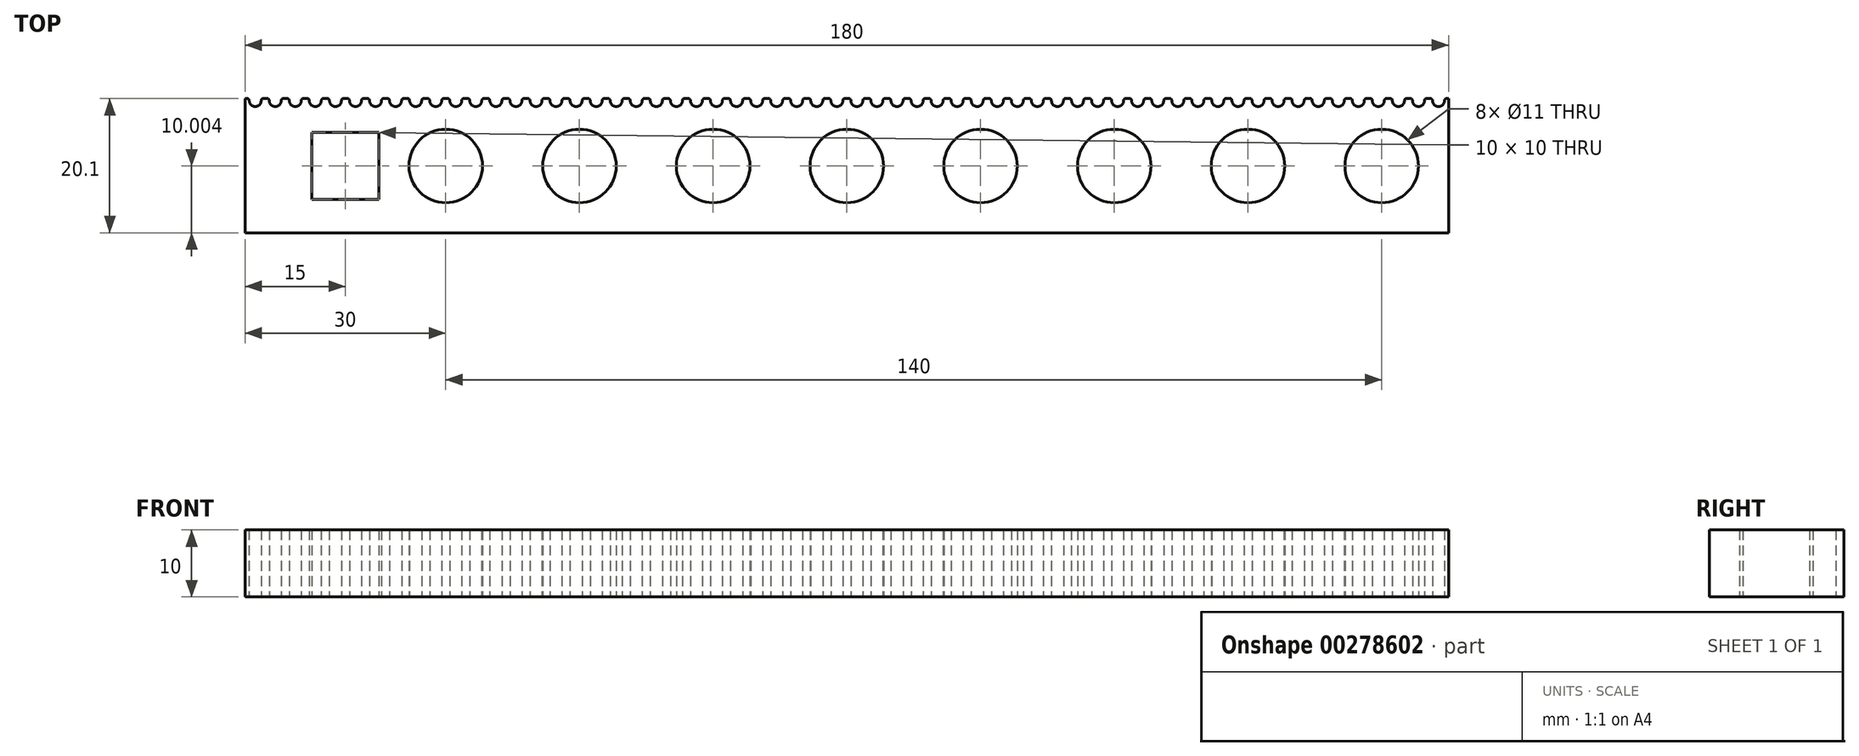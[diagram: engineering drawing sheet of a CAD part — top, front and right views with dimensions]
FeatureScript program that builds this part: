
annotation { "Feature Type Name" : "Feature", "Feature Type Description" : "" }
export const myFeature = defineFeature(function(context is Context, id is Id, definition is map)
    precondition{}
    {
        {
            var Q0;
            Q0=qCreatedBy(makeId("Top.planeOp"),FACE);
            var sketch = newSketch(context, id + "F0", { "sketchPlane" : qUnion([Q0])});
            skLineSegment(sketch, "E0.top", {"start": v(0, -20.1) * mm, "end": v(180, -20.1) * mm});
            skLineSegment(sketch, "E0.left", {"start": v(0, 0) * mm, "end": v(0, -20.1) * mm});
            skLineSegment(sketch, "E0.right", {"start": v(180, 0) * mm, "end": v(180, -20.1) * mm});
            skLineSegment(sketch, "E1", {"start": v(0, -1.2) * mm, "end": v(180, -1.2) * mm});
            skPoint(sketch, "E1.endSnap0", {"position": v(180, -10.05) * mm});
            skLineSegment(sketch, "E2", {"start": v(1.5, 2.44) * mm, "end": v(1.5, -3.97) * mm, "construction": true});
            skPoint(sketch, "E3", {"position": v(1.5, -1.2) * mm});
            skPoint(sketch, "E4", {"position": v(1.5, -0.3) * mm});
            skArc(sketch, "E5", {"start": v(0.6, -0.3) * mm, "mid": v(0.86, -0.94) * mm, "end": v(1.5, -1.2) * mm});
            skPoint(sketch, "E6", {"position": v(0.6, -0.3) * mm});
            skPoint(sketch, "E7", {"position": v(0.3, -0.3) * mm});
            skArc(sketch, "E8", {"start": v(0.6, -0.3) * mm, "mid": v(0.51, -0.09) * mm, "end": v(0.3, 0) * mm});
            skPoint(sketch, "E9", {"position": v(2.4, -0.3) * mm});
            skPoint(sketch, "E10", {"position": v(0.3, 0) * mm});
            skLineSegment(sketch, "E11", {"start": v(0.3, 0) * mm, "end": v(0, 0) * mm});
            skArc(sketch, "E12.MirrorCS", {"start": v(2.4, -0.3) * mm, "mid": v(2.14, -0.94) * mm, "end": v(1.5, -1.2) * mm});
            skArc(sketch, "E13.MirrorCS", {"start": v(2.4, -0.3) * mm, "mid": v(2.49, -0.09) * mm, "end": v(2.7, 0) * mm});
            skLineSegment(sketch, "E14.MirrorCS", {"start": v(2.7, 0) * mm, "end": v(3, 0) * mm});
            skLineSegment(sketch, "E15.1.0.0", {"start": v(3.3, 0) * mm, "end": v(3, 0) * mm});
            skArc(sketch, "E15.1.0.1", {"start": v(3.6, -0.3) * mm, "mid": v(3.51, -0.09) * mm, "end": v(3.3, 0) * mm});
            skArc(sketch, "E15.1.0.2", {"start": v(3.6, -0.3) * mm, "mid": v(3.86, -0.94) * mm, "end": v(4.5, -1.2) * mm});
            skArc(sketch, "E15.1.0.3", {"start": v(5.4, -0.3) * mm, "mid": v(5.14, -0.94) * mm, "end": v(4.5, -1.2) * mm});
            skArc(sketch, "E15.1.0.4", {"start": v(5.4, -0.3) * mm, "mid": v(5.49, -0.09) * mm, "end": v(5.7, 0) * mm});
            skLineSegment(sketch, "E15.1.0.5", {"start": v(5.7, 0) * mm, "end": v(6, 0) * mm});
            skLineSegment(sketch, "E15.2.0.0", {"start": v(6.3, 0) * mm, "end": v(6, 0) * mm});
            skArc(sketch, "E15.2.0.1", {"start": v(6.6, -0.3) * mm, "mid": v(6.51, -0.09) * mm, "end": v(6.3, 0) * mm});
            skArc(sketch, "E15.2.0.2", {"start": v(6.6, -0.3) * mm, "mid": v(6.86, -0.94) * mm, "end": v(7.5, -1.2) * mm});
            skArc(sketch, "E15.2.0.3", {"start": v(8.4, -0.3) * mm, "mid": v(8.14, -0.94) * mm, "end": v(7.5, -1.2) * mm});
            skArc(sketch, "E15.2.0.4", {"start": v(8.4, -0.3) * mm, "mid": v(8.49, -0.09) * mm, "end": v(8.7, 0) * mm});
            skLineSegment(sketch, "E15.2.0.5", {"start": v(8.7, 0) * mm, "end": v(9, 0) * mm});
            skLineSegment(sketch, "E15.3.0.0", {"start": v(9.3, 0) * mm, "end": v(9, 0) * mm});
            skArc(sketch, "E15.3.0.1", {"start": v(9.6, -0.3) * mm, "mid": v(9.51, -0.09) * mm, "end": v(9.3, 0) * mm});
            skArc(sketch, "E15.3.0.2", {"start": v(9.6, -0.3) * mm, "mid": v(9.86, -0.94) * mm, "end": v(10.5, -1.2) * mm});
            skArc(sketch, "E15.3.0.3", {"start": v(11.4, -0.3) * mm, "mid": v(11.14, -0.94) * mm, "end": v(10.5, -1.2) * mm});
            skArc(sketch, "E15.3.0.4", {"start": v(11.4, -0.3) * mm, "mid": v(11.49, -0.09) * mm, "end": v(11.7, 0) * mm});
            skLineSegment(sketch, "E15.3.0.5", {"start": v(11.7, 0) * mm, "end": v(12, 0) * mm});
            skLineSegment(sketch, "E15.4.0.0", {"start": v(12.3, 0) * mm, "end": v(12, 0) * mm});
            skArc(sketch, "E15.4.0.1", {"start": v(12.6, -0.3) * mm, "mid": v(12.51, -0.09) * mm, "end": v(12.3, 0) * mm});
            skArc(sketch, "E15.4.0.2", {"start": v(12.6, -0.3) * mm, "mid": v(12.86, -0.94) * mm, "end": v(13.5, -1.2) * mm});
            skArc(sketch, "E15.4.0.3", {"start": v(14.4, -0.3) * mm, "mid": v(14.14, -0.94) * mm, "end": v(13.5, -1.2) * mm});
            skArc(sketch, "E15.4.0.4", {"start": v(14.4, -0.3) * mm, "mid": v(14.49, -0.09) * mm, "end": v(14.7, 0) * mm});
            skLineSegment(sketch, "E15.4.0.5", {"start": v(14.7, 0) * mm, "end": v(15, 0) * mm});
            skLineSegment(sketch, "E15.5.0.0", {"start": v(15.3, 0) * mm, "end": v(15, 0) * mm});
            skArc(sketch, "E15.5.0.1", {"start": v(15.6, -0.3) * mm, "mid": v(15.51, -0.09) * mm, "end": v(15.3, 0) * mm});
            skArc(sketch, "E15.5.0.2", {"start": v(15.6, -0.3) * mm, "mid": v(15.86, -0.94) * mm, "end": v(16.5, -1.2) * mm});
            skArc(sketch, "E15.5.0.3", {"start": v(17.4, -0.3) * mm, "mid": v(17.14, -0.94) * mm, "end": v(16.5, -1.2) * mm});
            skArc(sketch, "E15.5.0.4", {"start": v(17.4, -0.3) * mm, "mid": v(17.49, -0.09) * mm, "end": v(17.7, 0) * mm});
            skLineSegment(sketch, "E15.5.0.5", {"start": v(17.7, 0) * mm, "end": v(18, 0) * mm});
            skLineSegment(sketch, "E15.6.0.0", {"start": v(18.3, 0) * mm, "end": v(18, 0) * mm});
            skArc(sketch, "E15.6.0.1", {"start": v(18.6, -0.3) * mm, "mid": v(18.51, -0.09) * mm, "end": v(18.3, 0) * mm});
            skArc(sketch, "E15.6.0.2", {"start": v(18.6, -0.3) * mm, "mid": v(18.86, -0.94) * mm, "end": v(19.5, -1.2) * mm});
            skArc(sketch, "E15.6.0.3", {"start": v(20.4, -0.3) * mm, "mid": v(20.14, -0.94) * mm, "end": v(19.5, -1.2) * mm});
            skArc(sketch, "E15.6.0.4", {"start": v(20.4, -0.3) * mm, "mid": v(20.49, -0.09) * mm, "end": v(20.7, 0) * mm});
            skLineSegment(sketch, "E15.6.0.5", {"start": v(20.7, 0) * mm, "end": v(21, 0) * mm});
            skLineSegment(sketch, "E15.7.0.0", {"start": v(21.3, 0) * mm, "end": v(21, 0) * mm});
            skArc(sketch, "E15.7.0.1", {"start": v(21.6, -0.3) * mm, "mid": v(21.51, -0.09) * mm, "end": v(21.3, 0) * mm});
            skArc(sketch, "E15.7.0.2", {"start": v(21.6, -0.3) * mm, "mid": v(21.86, -0.94) * mm, "end": v(22.5, -1.2) * mm});
            skArc(sketch, "E15.7.0.3", {"start": v(23.4, -0.3) * mm, "mid": v(23.14, -0.94) * mm, "end": v(22.5, -1.2) * mm});
            skArc(sketch, "E15.7.0.4", {"start": v(23.4, -0.3) * mm, "mid": v(23.49, -0.09) * mm, "end": v(23.7, 0) * mm});
            skLineSegment(sketch, "E15.7.0.5", {"start": v(23.7, 0) * mm, "end": v(24, 0) * mm});
            skLineSegment(sketch, "E15.8.0.0", {"start": v(24.3, 0) * mm, "end": v(24, 0) * mm});
            skArc(sketch, "E15.8.0.1", {"start": v(24.6, -0.3) * mm, "mid": v(24.51, -0.09) * mm, "end": v(24.3, 0) * mm});
            skArc(sketch, "E15.8.0.2", {"start": v(24.6, -0.3) * mm, "mid": v(24.86, -0.94) * mm, "end": v(25.5, -1.2) * mm});
            skArc(sketch, "E15.8.0.3", {"start": v(26.4, -0.3) * mm, "mid": v(26.14, -0.94) * mm, "end": v(25.5, -1.2) * mm});
            skArc(sketch, "E15.8.0.4", {"start": v(26.4, -0.3) * mm, "mid": v(26.49, -0.09) * mm, "end": v(26.7, 0) * mm});
            skLineSegment(sketch, "E15.8.0.5", {"start": v(26.7, 0) * mm, "end": v(27, 0) * mm});
            skLineSegment(sketch, "E15.9.0.0", {"start": v(27.3, 0) * mm, "end": v(27, 0) * mm});
            skArc(sketch, "E15.9.0.1", {"start": v(27.6, -0.3) * mm, "mid": v(27.51, -0.09) * mm, "end": v(27.3, 0) * mm});
            skArc(sketch, "E15.9.0.2", {"start": v(27.6, -0.3) * mm, "mid": v(27.86, -0.94) * mm, "end": v(28.5, -1.2) * mm});
            skArc(sketch, "E15.9.0.3", {"start": v(29.4, -0.3) * mm, "mid": v(29.14, -0.94) * mm, "end": v(28.5, -1.2) * mm});
            skArc(sketch, "E15.9.0.4", {"start": v(29.4, -0.3) * mm, "mid": v(29.49, -0.09) * mm, "end": v(29.7, 0) * mm});
            skLineSegment(sketch, "E15.9.0.5", {"start": v(29.7, 0) * mm, "end": v(30, 0) * mm});
            skLineSegment(sketch, "E15.10.0.0", {"start": v(30.3, 0) * mm, "end": v(30, 0) * mm});
            skArc(sketch, "E15.10.0.1", {"start": v(30.6, -0.3) * mm, "mid": v(30.51, -0.09) * mm, "end": v(30.3, 0) * mm});
            skArc(sketch, "E15.10.0.2", {"start": v(30.6, -0.3) * mm, "mid": v(30.86, -0.94) * mm, "end": v(31.5, -1.2) * mm});
            skArc(sketch, "E15.10.0.3", {"start": v(32.4, -0.3) * mm, "mid": v(32.14, -0.94) * mm, "end": v(31.5, -1.2) * mm});
            skArc(sketch, "E15.10.0.4", {"start": v(32.4, -0.3) * mm, "mid": v(32.49, -0.09) * mm, "end": v(32.7, 0) * mm});
            skLineSegment(sketch, "E15.10.0.5", {"start": v(32.7, 0) * mm, "end": v(33, 0) * mm});
            skLineSegment(sketch, "E15.11.0.0", {"start": v(33.3, 0) * mm, "end": v(33, 0) * mm});
            skArc(sketch, "E15.11.0.1", {"start": v(33.6, -0.3) * mm, "mid": v(33.51, -0.09) * mm, "end": v(33.3, 0) * mm});
            skArc(sketch, "E15.11.0.2", {"start": v(33.6, -0.3) * mm, "mid": v(33.86, -0.94) * mm, "end": v(34.5, -1.2) * mm});
            skArc(sketch, "E15.11.0.3", {"start": v(35.4, -0.3) * mm, "mid": v(35.14, -0.94) * mm, "end": v(34.5, -1.2) * mm});
            skArc(sketch, "E15.11.0.4", {"start": v(35.4, -0.3) * mm, "mid": v(35.49, -0.09) * mm, "end": v(35.7, 0) * mm});
            skLineSegment(sketch, "E15.11.0.5", {"start": v(35.7, 0) * mm, "end": v(36, 0) * mm});
            skLineSegment(sketch, "E15.12.0.0", {"start": v(36.3, 0) * mm, "end": v(36, 0) * mm});
            skArc(sketch, "E15.12.0.1", {"start": v(36.6, -0.3) * mm, "mid": v(36.51, -0.09) * mm, "end": v(36.3, 0) * mm});
            skArc(sketch, "E15.12.0.2", {"start": v(36.6, -0.3) * mm, "mid": v(36.86, -0.94) * mm, "end": v(37.5, -1.2) * mm});
            skArc(sketch, "E15.12.0.3", {"start": v(38.4, -0.3) * mm, "mid": v(38.14, -0.94) * mm, "end": v(37.5, -1.2) * mm});
            skArc(sketch, "E15.12.0.4", {"start": v(38.4, -0.3) * mm, "mid": v(38.49, -0.09) * mm, "end": v(38.7, 0) * mm});
            skLineSegment(sketch, "E15.12.0.5", {"start": v(38.7, 0) * mm, "end": v(39, 0) * mm});
            skLineSegment(sketch, "E15.13.0.0", {"start": v(39.3, 0) * mm, "end": v(39, 0) * mm});
            skArc(sketch, "E15.13.0.1", {"start": v(39.6, -0.3) * mm, "mid": v(39.51, -0.09) * mm, "end": v(39.3, 0) * mm});
            skArc(sketch, "E15.13.0.2", {"start": v(39.6, -0.3) * mm, "mid": v(39.86, -0.94) * mm, "end": v(40.5, -1.2) * mm});
            skArc(sketch, "E15.13.0.3", {"start": v(41.4, -0.3) * mm, "mid": v(41.14, -0.94) * mm, "end": v(40.5, -1.2) * mm});
            skArc(sketch, "E15.13.0.4", {"start": v(41.4, -0.3) * mm, "mid": v(41.49, -0.09) * mm, "end": v(41.7, 0) * mm});
            skLineSegment(sketch, "E15.13.0.5", {"start": v(41.7, 0) * mm, "end": v(42, 0) * mm});
            skLineSegment(sketch, "E15.14.0.0", {"start": v(42.3, 0) * mm, "end": v(42, 0) * mm});
            skArc(sketch, "E15.14.0.1", {"start": v(42.6, -0.3) * mm, "mid": v(42.51, -0.09) * mm, "end": v(42.3, 0) * mm});
            skArc(sketch, "E15.14.0.2", {"start": v(42.6, -0.3) * mm, "mid": v(42.86, -0.94) * mm, "end": v(43.5, -1.2) * mm});
            skArc(sketch, "E15.14.0.3", {"start": v(44.4, -0.3) * mm, "mid": v(44.14, -0.94) * mm, "end": v(43.5, -1.2) * mm});
            skArc(sketch, "E15.14.0.4", {"start": v(44.4, -0.3) * mm, "mid": v(44.49, -0.09) * mm, "end": v(44.7, 0) * mm});
            skLineSegment(sketch, "E15.14.0.5", {"start": v(44.7, 0) * mm, "end": v(45, 0) * mm});
            skLineSegment(sketch, "E15.15.0.0", {"start": v(45.3, 0) * mm, "end": v(45, 0) * mm});
            skArc(sketch, "E15.15.0.1", {"start": v(45.6, -0.3) * mm, "mid": v(45.51, -0.09) * mm, "end": v(45.3, 0) * mm});
            skArc(sketch, "E15.15.0.2", {"start": v(45.6, -0.3) * mm, "mid": v(45.86, -0.94) * mm, "end": v(46.5, -1.2) * mm});
            skArc(sketch, "E15.15.0.3", {"start": v(47.4, -0.3) * mm, "mid": v(47.14, -0.94) * mm, "end": v(46.5, -1.2) * mm});
            skArc(sketch, "E15.15.0.4", {"start": v(47.4, -0.3) * mm, "mid": v(47.49, -0.09) * mm, "end": v(47.7, 0) * mm});
            skLineSegment(sketch, "E15.15.0.5", {"start": v(47.7, 0) * mm, "end": v(48, 0) * mm});
            skLineSegment(sketch, "E15.16.0.0", {"start": v(48.3, 0) * mm, "end": v(48, 0) * mm});
            skArc(sketch, "E15.16.0.1", {"start": v(48.6, -0.3) * mm, "mid": v(48.51, -0.09) * mm, "end": v(48.3, 0) * mm});
            skArc(sketch, "E15.16.0.2", {"start": v(48.6, -0.3) * mm, "mid": v(48.86, -0.94) * mm, "end": v(49.5, -1.2) * mm});
            skArc(sketch, "E15.16.0.3", {"start": v(50.4, -0.3) * mm, "mid": v(50.14, -0.94) * mm, "end": v(49.5, -1.2) * mm});
            skArc(sketch, "E15.16.0.4", {"start": v(50.4, -0.3) * mm, "mid": v(50.49, -0.09) * mm, "end": v(50.7, 0) * mm});
            skLineSegment(sketch, "E15.16.0.5", {"start": v(50.7, 0) * mm, "end": v(51, 0) * mm});
            skLineSegment(sketch, "E15.17.0.0", {"start": v(51.3, 0) * mm, "end": v(51, 0) * mm});
            skArc(sketch, "E15.17.0.1", {"start": v(51.6, -0.3) * mm, "mid": v(51.51, -0.09) * mm, "end": v(51.3, 0) * mm});
            skArc(sketch, "E15.17.0.2", {"start": v(51.6, -0.3) * mm, "mid": v(51.86, -0.94) * mm, "end": v(52.5, -1.2) * mm});
            skArc(sketch, "E15.17.0.3", {"start": v(53.4, -0.3) * mm, "mid": v(53.14, -0.94) * mm, "end": v(52.5, -1.2) * mm});
            skArc(sketch, "E15.17.0.4", {"start": v(53.4, -0.3) * mm, "mid": v(53.49, -0.09) * mm, "end": v(53.7, 0) * mm});
            skLineSegment(sketch, "E15.17.0.5", {"start": v(53.7, 0) * mm, "end": v(54, 0) * mm});
            skLineSegment(sketch, "E15.18.0.0", {"start": v(54.3, 0) * mm, "end": v(54, 0) * mm});
            skArc(sketch, "E15.18.0.1", {"start": v(54.6, -0.3) * mm, "mid": v(54.51, -0.09) * mm, "end": v(54.3, 0) * mm});
            skArc(sketch, "E15.18.0.2", {"start": v(54.6, -0.3) * mm, "mid": v(54.86, -0.94) * mm, "end": v(55.5, -1.2) * mm});
            skArc(sketch, "E15.18.0.3", {"start": v(56.4, -0.3) * mm, "mid": v(56.14, -0.94) * mm, "end": v(55.5, -1.2) * mm});
            skArc(sketch, "E15.18.0.4", {"start": v(56.4, -0.3) * mm, "mid": v(56.49, -0.09) * mm, "end": v(56.7, 0) * mm});
            skLineSegment(sketch, "E15.18.0.5", {"start": v(56.7, 0) * mm, "end": v(57, 0) * mm});
            skLineSegment(sketch, "E15.19.0.0", {"start": v(57.3, 0) * mm, "end": v(57, 0) * mm});
            skArc(sketch, "E15.19.0.1", {"start": v(57.6, -0.3) * mm, "mid": v(57.51, -0.09) * mm, "end": v(57.3, 0) * mm});
            skArc(sketch, "E15.19.0.2", {"start": v(57.6, -0.3) * mm, "mid": v(57.86, -0.94) * mm, "end": v(58.5, -1.2) * mm});
            skArc(sketch, "E15.19.0.3", {"start": v(59.4, -0.3) * mm, "mid": v(59.14, -0.94) * mm, "end": v(58.5, -1.2) * mm});
            skArc(sketch, "E15.19.0.4", {"start": v(59.4, -0.3) * mm, "mid": v(59.49, -0.09) * mm, "end": v(59.7, 0) * mm});
            skLineSegment(sketch, "E15.19.0.5", {"start": v(59.7, 0) * mm, "end": v(60, 0) * mm});
            skLineSegment(sketch, "E15.20.0.0", {"start": v(60.3, 0) * mm, "end": v(60, 0) * mm});
            skArc(sketch, "E15.20.0.1", {"start": v(60.6, -0.3) * mm, "mid": v(60.51, -0.09) * mm, "end": v(60.3, 0) * mm});
            skArc(sketch, "E15.20.0.2", {"start": v(60.6, -0.3) * mm, "mid": v(60.86, -0.94) * mm, "end": v(61.5, -1.2) * mm});
            skArc(sketch, "E15.20.0.3", {"start": v(62.4, -0.3) * mm, "mid": v(62.14, -0.94) * mm, "end": v(61.5, -1.2) * mm});
            skArc(sketch, "E15.20.0.4", {"start": v(62.4, -0.3) * mm, "mid": v(62.49, -0.09) * mm, "end": v(62.7, 0) * mm});
            skLineSegment(sketch, "E15.20.0.5", {"start": v(62.7, 0) * mm, "end": v(63, 0) * mm});
            skLineSegment(sketch, "E15.21.0.0", {"start": v(63.3, 0) * mm, "end": v(63, 0) * mm});
            skArc(sketch, "E15.21.0.1", {"start": v(63.6, -0.3) * mm, "mid": v(63.51, -0.09) * mm, "end": v(63.3, 0) * mm});
            skArc(sketch, "E15.21.0.2", {"start": v(63.6, -0.3) * mm, "mid": v(63.86, -0.94) * mm, "end": v(64.5, -1.2) * mm});
            skArc(sketch, "E15.21.0.3", {"start": v(65.4, -0.3) * mm, "mid": v(65.14, -0.94) * mm, "end": v(64.5, -1.2) * mm});
            skArc(sketch, "E15.21.0.4", {"start": v(65.4, -0.3) * mm, "mid": v(65.49, -0.09) * mm, "end": v(65.7, 0) * mm});
            skLineSegment(sketch, "E15.21.0.5", {"start": v(65.7, 0) * mm, "end": v(66, 0) * mm});
            skLineSegment(sketch, "E15.22.0.0", {"start": v(66.3, 0) * mm, "end": v(66, 0) * mm});
            skArc(sketch, "E15.22.0.1", {"start": v(66.6, -0.3) * mm, "mid": v(66.51, -0.09) * mm, "end": v(66.3, 0) * mm});
            skArc(sketch, "E15.22.0.2", {"start": v(66.6, -0.3) * mm, "mid": v(66.86, -0.94) * mm, "end": v(67.5, -1.2) * mm});
            skArc(sketch, "E15.22.0.3", {"start": v(68.4, -0.3) * mm, "mid": v(68.14, -0.94) * mm, "end": v(67.5, -1.2) * mm});
            skArc(sketch, "E15.22.0.4", {"start": v(68.4, -0.3) * mm, "mid": v(68.49, -0.09) * mm, "end": v(68.7, 0) * mm});
            skLineSegment(sketch, "E15.22.0.5", {"start": v(68.7, 0) * mm, "end": v(69, 0) * mm});
            skLineSegment(sketch, "E15.23.0.0", {"start": v(69.3, 0) * mm, "end": v(69, 0) * mm});
            skArc(sketch, "E15.23.0.1", {"start": v(69.6, -0.3) * mm, "mid": v(69.51, -0.09) * mm, "end": v(69.3, 0) * mm});
            skArc(sketch, "E15.23.0.2", {"start": v(69.6, -0.3) * mm, "mid": v(69.86, -0.94) * mm, "end": v(70.5, -1.2) * mm});
            skArc(sketch, "E15.23.0.3", {"start": v(71.4, -0.3) * mm, "mid": v(71.14, -0.94) * mm, "end": v(70.5, -1.2) * mm});
            skArc(sketch, "E15.23.0.4", {"start": v(71.4, -0.3) * mm, "mid": v(71.49, -0.09) * mm, "end": v(71.7, 0) * mm});
            skLineSegment(sketch, "E15.23.0.5", {"start": v(71.7, 0) * mm, "end": v(72, 0) * mm});
            skLineSegment(sketch, "E15.24.0.0", {"start": v(72.3, 0) * mm, "end": v(72, 0) * mm});
            skArc(sketch, "E15.24.0.1", {"start": v(72.6, -0.3) * mm, "mid": v(72.51, -0.09) * mm, "end": v(72.3, 0) * mm});
            skArc(sketch, "E15.24.0.2", {"start": v(72.6, -0.3) * mm, "mid": v(72.86, -0.94) * mm, "end": v(73.5, -1.2) * mm});
            skArc(sketch, "E15.24.0.3", {"start": v(74.4, -0.3) * mm, "mid": v(74.14, -0.94) * mm, "end": v(73.5, -1.2) * mm});
            skArc(sketch, "E15.24.0.4", {"start": v(74.4, -0.3) * mm, "mid": v(74.49, -0.09) * mm, "end": v(74.7, 0) * mm});
            skLineSegment(sketch, "E15.24.0.5", {"start": v(74.7, 0) * mm, "end": v(75, 0) * mm});
            skLineSegment(sketch, "E15.25.0.0", {"start": v(75.3, 0) * mm, "end": v(75, 0) * mm});
            skArc(sketch, "E15.25.0.1", {"start": v(75.6, -0.3) * mm, "mid": v(75.51, -0.09) * mm, "end": v(75.3, 0) * mm});
            skArc(sketch, "E15.25.0.2", {"start": v(75.6, -0.3) * mm, "mid": v(75.86, -0.94) * mm, "end": v(76.5, -1.2) * mm});
            skArc(sketch, "E15.25.0.3", {"start": v(77.4, -0.3) * mm, "mid": v(77.14, -0.94) * mm, "end": v(76.5, -1.2) * mm});
            skArc(sketch, "E15.25.0.4", {"start": v(77.4, -0.3) * mm, "mid": v(77.49, -0.09) * mm, "end": v(77.7, 0) * mm});
            skLineSegment(sketch, "E15.25.0.5", {"start": v(77.7, 0) * mm, "end": v(78, 0) * mm});
            skLineSegment(sketch, "E15.26.0.0", {"start": v(78.3, 0) * mm, "end": v(78, 0) * mm});
            skArc(sketch, "E15.26.0.1", {"start": v(78.6, -0.3) * mm, "mid": v(78.51, -0.09) * mm, "end": v(78.3, 0) * mm});
            skArc(sketch, "E15.26.0.2", {"start": v(78.6, -0.3) * mm, "mid": v(78.86, -0.94) * mm, "end": v(79.5, -1.2) * mm});
            skArc(sketch, "E15.26.0.3", {"start": v(80.4, -0.3) * mm, "mid": v(80.14, -0.94) * mm, "end": v(79.5, -1.2) * mm});
            skArc(sketch, "E15.26.0.4", {"start": v(80.4, -0.3) * mm, "mid": v(80.49, -0.09) * mm, "end": v(80.7, 0) * mm});
            skLineSegment(sketch, "E15.26.0.5", {"start": v(80.7, 0) * mm, "end": v(81, 0) * mm});
            skLineSegment(sketch, "E15.27.0.0", {"start": v(81.3, 0) * mm, "end": v(81, 0) * mm});
            skArc(sketch, "E15.27.0.1", {"start": v(81.6, -0.3) * mm, "mid": v(81.51, -0.09) * mm, "end": v(81.3, 0) * mm});
            skArc(sketch, "E15.27.0.2", {"start": v(81.6, -0.3) * mm, "mid": v(81.86, -0.94) * mm, "end": v(82.5, -1.2) * mm});
            skArc(sketch, "E15.27.0.3", {"start": v(83.4, -0.3) * mm, "mid": v(83.14, -0.94) * mm, "end": v(82.5, -1.2) * mm});
            skArc(sketch, "E15.27.0.4", {"start": v(83.4, -0.3) * mm, "mid": v(83.49, -0.09) * mm, "end": v(83.7, 0) * mm});
            skLineSegment(sketch, "E15.27.0.5", {"start": v(83.7, 0) * mm, "end": v(84, 0) * mm});
            skLineSegment(sketch, "E15.28.0.0", {"start": v(84.3, 0) * mm, "end": v(84, 0) * mm});
            skArc(sketch, "E15.28.0.1", {"start": v(84.6, -0.3) * mm, "mid": v(84.51, -0.09) * mm, "end": v(84.3, 0) * mm});
            skArc(sketch, "E15.28.0.2", {"start": v(84.6, -0.3) * mm, "mid": v(84.86, -0.94) * mm, "end": v(85.5, -1.2) * mm});
            skArc(sketch, "E15.28.0.3", {"start": v(86.4, -0.3) * mm, "mid": v(86.14, -0.94) * mm, "end": v(85.5, -1.2) * mm});
            skArc(sketch, "E15.28.0.4", {"start": v(86.4, -0.3) * mm, "mid": v(86.49, -0.09) * mm, "end": v(86.7, 0) * mm});
            skLineSegment(sketch, "E15.28.0.5", {"start": v(86.7, 0) * mm, "end": v(87, 0) * mm});
            skLineSegment(sketch, "E15.29.0.0", {"start": v(87.3, 0) * mm, "end": v(87, 0) * mm});
            skArc(sketch, "E15.29.0.1", {"start": v(87.6, -0.3) * mm, "mid": v(87.51, -0.09) * mm, "end": v(87.3, 0) * mm});
            skArc(sketch, "E15.29.0.2", {"start": v(87.6, -0.3) * mm, "mid": v(87.86, -0.94) * mm, "end": v(88.5, -1.2) * mm});
            skArc(sketch, "E15.29.0.3", {"start": v(89.4, -0.3) * mm, "mid": v(89.14, -0.94) * mm, "end": v(88.5, -1.2) * mm});
            skArc(sketch, "E15.29.0.4", {"start": v(89.4, -0.3) * mm, "mid": v(89.49, -0.09) * mm, "end": v(89.7, 0) * mm});
            skLineSegment(sketch, "E15.29.0.5", {"start": v(89.7, 0) * mm, "end": v(90, 0) * mm});
            skLineSegment(sketch, "E15.30.0.0", {"start": v(90.3, 0) * mm, "end": v(90, 0) * mm});
            skArc(sketch, "E15.30.0.1", {"start": v(90.6, -0.3) * mm, "mid": v(90.51, -0.09) * mm, "end": v(90.3, 0) * mm});
            skArc(sketch, "E15.30.0.2", {"start": v(90.6, -0.3) * mm, "mid": v(90.86, -0.94) * mm, "end": v(91.5, -1.2) * mm});
            skArc(sketch, "E15.30.0.3", {"start": v(92.4, -0.3) * mm, "mid": v(92.14, -0.94) * mm, "end": v(91.5, -1.2) * mm});
            skArc(sketch, "E15.30.0.4", {"start": v(92.4, -0.3) * mm, "mid": v(92.49, -0.09) * mm, "end": v(92.7, 0) * mm});
            skLineSegment(sketch, "E15.30.0.5", {"start": v(92.7, 0) * mm, "end": v(93, 0) * mm});
            skLineSegment(sketch, "E15.31.0.0", {"start": v(93.3, 0) * mm, "end": v(93, 0) * mm});
            skArc(sketch, "E15.31.0.1", {"start": v(93.6, -0.3) * mm, "mid": v(93.51, -0.09) * mm, "end": v(93.3, 0) * mm});
            skArc(sketch, "E15.31.0.2", {"start": v(93.6, -0.3) * mm, "mid": v(93.86, -0.94) * mm, "end": v(94.5, -1.2) * mm});
            skArc(sketch, "E15.31.0.3", {"start": v(95.4, -0.3) * mm, "mid": v(95.14, -0.94) * mm, "end": v(94.5, -1.2) * mm});
            skArc(sketch, "E15.31.0.4", {"start": v(95.4, -0.3) * mm, "mid": v(95.49, -0.09) * mm, "end": v(95.7, 0) * mm});
            skLineSegment(sketch, "E15.31.0.5", {"start": v(95.7, 0) * mm, "end": v(96, 0) * mm});
            skLineSegment(sketch, "E15.32.0.0", {"start": v(96.3, 0) * mm, "end": v(96, 0) * mm});
            skArc(sketch, "E15.32.0.1", {"start": v(96.6, -0.3) * mm, "mid": v(96.51, -0.09) * mm, "end": v(96.3, 0) * mm});
            skArc(sketch, "E15.32.0.2", {"start": v(96.6, -0.3) * mm, "mid": v(96.86, -0.94) * mm, "end": v(97.5, -1.2) * mm});
            skArc(sketch, "E15.32.0.3", {"start": v(98.4, -0.3) * mm, "mid": v(98.14, -0.94) * mm, "end": v(97.5, -1.2) * mm});
            skArc(sketch, "E15.32.0.4", {"start": v(98.4, -0.3) * mm, "mid": v(98.49, -0.09) * mm, "end": v(98.7, 0) * mm});
            skLineSegment(sketch, "E15.32.0.5", {"start": v(98.7, 0) * mm, "end": v(99, 0) * mm});
            skLineSegment(sketch, "E15.33.0.0", {"start": v(99.3, 0) * mm, "end": v(99, 0) * mm});
            skArc(sketch, "E15.33.0.1", {"start": v(99.6, -0.3) * mm, "mid": v(99.51, -0.09) * mm, "end": v(99.3, 0) * mm});
            skArc(sketch, "E15.33.0.2", {"start": v(99.6, -0.3) * mm, "mid": v(99.86, -0.94) * mm, "end": v(100.5, -1.2) * mm});
            skArc(sketch, "E15.33.0.3", {"start": v(101.4, -0.3) * mm, "mid": v(101.14, -0.94) * mm, "end": v(100.5, -1.2) * mm});
            skArc(sketch, "E15.33.0.4", {"start": v(101.4, -0.3) * mm, "mid": v(101.49, -0.09) * mm, "end": v(101.7, 0) * mm});
            skLineSegment(sketch, "E15.33.0.5", {"start": v(101.7, 0) * mm, "end": v(102, 0) * mm});
            skLineSegment(sketch, "E15.34.0.0", {"start": v(102.3, 0) * mm, "end": v(102, 0) * mm});
            skArc(sketch, "E15.34.0.1", {"start": v(102.6, -0.3) * mm, "mid": v(102.51, -0.09) * mm, "end": v(102.3, 0) * mm});
            skArc(sketch, "E15.34.0.2", {"start": v(102.6, -0.3) * mm, "mid": v(102.86, -0.94) * mm, "end": v(103.5, -1.2) * mm});
            skArc(sketch, "E15.34.0.3", {"start": v(104.4, -0.3) * mm, "mid": v(104.14, -0.94) * mm, "end": v(103.5, -1.2) * mm});
            skArc(sketch, "E15.34.0.4", {"start": v(104.4, -0.3) * mm, "mid": v(104.49, -0.09) * mm, "end": v(104.7, 0) * mm});
            skLineSegment(sketch, "E15.34.0.5", {"start": v(104.7, 0) * mm, "end": v(105, 0) * mm});
            skLineSegment(sketch, "E15.35.0.0", {"start": v(105.3, 0) * mm, "end": v(105, 0) * mm});
            skArc(sketch, "E15.35.0.1", {"start": v(105.6, -0.3) * mm, "mid": v(105.51, -0.09) * mm, "end": v(105.3, 0) * mm});
            skArc(sketch, "E15.35.0.2", {"start": v(105.6, -0.3) * mm, "mid": v(105.86, -0.94) * mm, "end": v(106.5, -1.2) * mm});
            skArc(sketch, "E15.35.0.3", {"start": v(107.4, -0.3) * mm, "mid": v(107.14, -0.94) * mm, "end": v(106.5, -1.2) * mm});
            skArc(sketch, "E15.35.0.4", {"start": v(107.4, -0.3) * mm, "mid": v(107.49, -0.09) * mm, "end": v(107.7, 0) * mm});
            skLineSegment(sketch, "E15.35.0.5", {"start": v(107.7, 0) * mm, "end": v(108, 0) * mm});
            skLineSegment(sketch, "E15.36.0.0", {"start": v(108.3, 0) * mm, "end": v(108, 0) * mm});
            skArc(sketch, "E15.36.0.1", {"start": v(108.6, -0.3) * mm, "mid": v(108.51, -0.09) * mm, "end": v(108.3, 0) * mm});
            skArc(sketch, "E15.36.0.2", {"start": v(108.6, -0.3) * mm, "mid": v(108.86, -0.94) * mm, "end": v(109.5, -1.2) * mm});
            skArc(sketch, "E15.36.0.3", {"start": v(110.4, -0.3) * mm, "mid": v(110.14, -0.94) * mm, "end": v(109.5, -1.2) * mm});
            skArc(sketch, "E15.36.0.4", {"start": v(110.4, -0.3) * mm, "mid": v(110.49, -0.09) * mm, "end": v(110.7, 0) * mm});
            skLineSegment(sketch, "E15.36.0.5", {"start": v(110.7, 0) * mm, "end": v(111, 0) * mm});
            skLineSegment(sketch, "E15.37.0.0", {"start": v(111.3, 0) * mm, "end": v(111, 0) * mm});
            skArc(sketch, "E15.37.0.1", {"start": v(111.6, -0.3) * mm, "mid": v(111.51, -0.09) * mm, "end": v(111.3, 0) * mm});
            skArc(sketch, "E15.37.0.2", {"start": v(111.6, -0.3) * mm, "mid": v(111.86, -0.94) * mm, "end": v(112.5, -1.2) * mm});
            skArc(sketch, "E15.37.0.3", {"start": v(113.4, -0.3) * mm, "mid": v(113.14, -0.94) * mm, "end": v(112.5, -1.2) * mm});
            skArc(sketch, "E15.37.0.4", {"start": v(113.4, -0.3) * mm, "mid": v(113.49, -0.09) * mm, "end": v(113.7, 0) * mm});
            skLineSegment(sketch, "E15.37.0.5", {"start": v(113.7, 0) * mm, "end": v(114, 0) * mm});
            skLineSegment(sketch, "E15.38.0.0", {"start": v(114.3, 0) * mm, "end": v(114, 0) * mm});
            skArc(sketch, "E15.38.0.1", {"start": v(114.6, -0.3) * mm, "mid": v(114.51, -0.09) * mm, "end": v(114.3, 0) * mm});
            skArc(sketch, "E15.38.0.2", {"start": v(114.6, -0.3) * mm, "mid": v(114.86, -0.94) * mm, "end": v(115.5, -1.2) * mm});
            skArc(sketch, "E15.38.0.3", {"start": v(116.4, -0.3) * mm, "mid": v(116.14, -0.94) * mm, "end": v(115.5, -1.2) * mm});
            skArc(sketch, "E15.38.0.4", {"start": v(116.4, -0.3) * mm, "mid": v(116.49, -0.09) * mm, "end": v(116.7, 0) * mm});
            skLineSegment(sketch, "E15.38.0.5", {"start": v(116.7, 0) * mm, "end": v(117, 0) * mm});
            skLineSegment(sketch, "E15.39.0.0", {"start": v(117.3, 0) * mm, "end": v(117, 0) * mm});
            skArc(sketch, "E15.39.0.1", {"start": v(117.6, -0.3) * mm, "mid": v(117.51, -0.09) * mm, "end": v(117.3, 0) * mm});
            skArc(sketch, "E15.39.0.2", {"start": v(117.6, -0.3) * mm, "mid": v(117.86, -0.94) * mm, "end": v(118.5, -1.2) * mm});
            skArc(sketch, "E15.39.0.3", {"start": v(119.4, -0.3) * mm, "mid": v(119.14, -0.94) * mm, "end": v(118.5, -1.2) * mm});
            skArc(sketch, "E15.39.0.4", {"start": v(119.4, -0.3) * mm, "mid": v(119.49, -0.09) * mm, "end": v(119.7, 0) * mm});
            skLineSegment(sketch, "E15.39.0.5", {"start": v(119.7, 0) * mm, "end": v(120, 0) * mm});
            skLineSegment(sketch, "E15.40.0.0", {"start": v(120.3, 0) * mm, "end": v(120, 0) * mm});
            skArc(sketch, "E15.40.0.1", {"start": v(120.6, -0.3) * mm, "mid": v(120.51, -0.09) * mm, "end": v(120.3, 0) * mm});
            skArc(sketch, "E15.40.0.2", {"start": v(120.6, -0.3) * mm, "mid": v(120.86, -0.94) * mm, "end": v(121.5, -1.2) * mm});
            skArc(sketch, "E15.40.0.3", {"start": v(122.4, -0.3) * mm, "mid": v(122.14, -0.94) * mm, "end": v(121.5, -1.2) * mm});
            skArc(sketch, "E15.40.0.4", {"start": v(122.4, -0.3) * mm, "mid": v(122.49, -0.09) * mm, "end": v(122.7, 0) * mm});
            skLineSegment(sketch, "E15.40.0.5", {"start": v(122.7, 0) * mm, "end": v(123, 0) * mm});
            skLineSegment(sketch, "E15.41.0.0", {"start": v(123.3, 0) * mm, "end": v(123, 0) * mm});
            skArc(sketch, "E15.41.0.1", {"start": v(123.6, -0.3) * mm, "mid": v(123.51, -0.09) * mm, "end": v(123.3, 0) * mm});
            skArc(sketch, "E15.41.0.2", {"start": v(123.6, -0.3) * mm, "mid": v(123.86, -0.94) * mm, "end": v(124.5, -1.2) * mm});
            skArc(sketch, "E15.41.0.3", {"start": v(125.4, -0.3) * mm, "mid": v(125.14, -0.94) * mm, "end": v(124.5, -1.2) * mm});
            skArc(sketch, "E15.41.0.4", {"start": v(125.4, -0.3) * mm, "mid": v(125.49, -0.09) * mm, "end": v(125.7, 0) * mm});
            skLineSegment(sketch, "E15.41.0.5", {"start": v(125.7, 0) * mm, "end": v(126, 0) * mm});
            skLineSegment(sketch, "E15.42.0.0", {"start": v(126.3, 0) * mm, "end": v(126, 0) * mm});
            skArc(sketch, "E15.42.0.1", {"start": v(126.6, -0.3) * mm, "mid": v(126.51, -0.09) * mm, "end": v(126.3, 0) * mm});
            skArc(sketch, "E15.42.0.2", {"start": v(126.6, -0.3) * mm, "mid": v(126.86, -0.94) * mm, "end": v(127.5, -1.2) * mm});
            skArc(sketch, "E15.42.0.3", {"start": v(128.4, -0.3) * mm, "mid": v(128.14, -0.94) * mm, "end": v(127.5, -1.2) * mm});
            skArc(sketch, "E15.42.0.4", {"start": v(128.4, -0.3) * mm, "mid": v(128.49, -0.09) * mm, "end": v(128.7, 0) * mm});
            skLineSegment(sketch, "E15.42.0.5", {"start": v(128.7, 0) * mm, "end": v(129, 0) * mm});
            skLineSegment(sketch, "E15.43.0.0", {"start": v(129.3, 0) * mm, "end": v(129, 0) * mm});
            skArc(sketch, "E15.43.0.1", {"start": v(129.6, -0.3) * mm, "mid": v(129.51, -0.09) * mm, "end": v(129.3, 0) * mm});
            skArc(sketch, "E15.43.0.2", {"start": v(129.6, -0.3) * mm, "mid": v(129.86, -0.94) * mm, "end": v(130.5, -1.2) * mm});
            skArc(sketch, "E15.43.0.3", {"start": v(131.4, -0.3) * mm, "mid": v(131.14, -0.94) * mm, "end": v(130.5, -1.2) * mm});
            skArc(sketch, "E15.43.0.4", {"start": v(131.4, -0.3) * mm, "mid": v(131.49, -0.09) * mm, "end": v(131.7, 0) * mm});
            skLineSegment(sketch, "E15.43.0.5", {"start": v(131.7, 0) * mm, "end": v(132, 0) * mm});
            skLineSegment(sketch, "E15.44.0.0", {"start": v(132.3, 0) * mm, "end": v(132, 0) * mm});
            skArc(sketch, "E15.44.0.1", {"start": v(132.6, -0.3) * mm, "mid": v(132.51, -0.09) * mm, "end": v(132.3, 0) * mm});
            skArc(sketch, "E15.44.0.2", {"start": v(132.6, -0.3) * mm, "mid": v(132.86, -0.94) * mm, "end": v(133.5, -1.2) * mm});
            skArc(sketch, "E15.44.0.3", {"start": v(134.4, -0.3) * mm, "mid": v(134.14, -0.94) * mm, "end": v(133.5, -1.2) * mm});
            skArc(sketch, "E15.44.0.4", {"start": v(134.4, -0.3) * mm, "mid": v(134.49, -0.09) * mm, "end": v(134.7, 0) * mm});
            skLineSegment(sketch, "E15.44.0.5", {"start": v(134.7, 0) * mm, "end": v(135, 0) * mm});
            skLineSegment(sketch, "E15.45.0.0", {"start": v(135.3, 0) * mm, "end": v(135, 0) * mm});
            skArc(sketch, "E15.45.0.1", {"start": v(135.6, -0.3) * mm, "mid": v(135.51, -0.09) * mm, "end": v(135.3, 0) * mm});
            skArc(sketch, "E15.45.0.2", {"start": v(135.6, -0.3) * mm, "mid": v(135.86, -0.94) * mm, "end": v(136.5, -1.2) * mm});
            skArc(sketch, "E15.45.0.3", {"start": v(137.4, -0.3) * mm, "mid": v(137.14, -0.94) * mm, "end": v(136.5, -1.2) * mm});
            skArc(sketch, "E15.45.0.4", {"start": v(137.4, -0.3) * mm, "mid": v(137.49, -0.09) * mm, "end": v(137.7, 0) * mm});
            skLineSegment(sketch, "E15.45.0.5", {"start": v(137.7, 0) * mm, "end": v(138, 0) * mm});
            skLineSegment(sketch, "E15.46.0.0", {"start": v(138.3, 0) * mm, "end": v(138, 0) * mm});
            skArc(sketch, "E15.46.0.1", {"start": v(138.6, -0.3) * mm, "mid": v(138.51, -0.09) * mm, "end": v(138.3, 0) * mm});
            skArc(sketch, "E15.46.0.2", {"start": v(138.6, -0.3) * mm, "mid": v(138.86, -0.94) * mm, "end": v(139.5, -1.2) * mm});
            skArc(sketch, "E15.46.0.3", {"start": v(140.4, -0.3) * mm, "mid": v(140.14, -0.94) * mm, "end": v(139.5, -1.2) * mm});
            skArc(sketch, "E15.46.0.4", {"start": v(140.4, -0.3) * mm, "mid": v(140.49, -0.09) * mm, "end": v(140.7, 0) * mm});
            skLineSegment(sketch, "E15.46.0.5", {"start": v(140.7, 0) * mm, "end": v(141, 0) * mm});
            skLineSegment(sketch, "E15.47.0.0", {"start": v(141.3, 0) * mm, "end": v(141, 0) * mm});
            skArc(sketch, "E15.47.0.1", {"start": v(141.6, -0.3) * mm, "mid": v(141.51, -0.09) * mm, "end": v(141.3, 0) * mm});
            skArc(sketch, "E15.47.0.2", {"start": v(141.6, -0.3) * mm, "mid": v(141.86, -0.94) * mm, "end": v(142.5, -1.2) * mm});
            skArc(sketch, "E15.47.0.3", {"start": v(143.4, -0.3) * mm, "mid": v(143.14, -0.94) * mm, "end": v(142.5, -1.2) * mm});
            skArc(sketch, "E15.47.0.4", {"start": v(143.4, -0.3) * mm, "mid": v(143.49, -0.09) * mm, "end": v(143.7, 0) * mm});
            skLineSegment(sketch, "E15.47.0.5", {"start": v(143.7, 0) * mm, "end": v(144, 0) * mm});
            skLineSegment(sketch, "E15.48.0.0", {"start": v(144.3, 0) * mm, "end": v(144, 0) * mm});
            skArc(sketch, "E15.48.0.1", {"start": v(144.6, -0.3) * mm, "mid": v(144.51, -0.09) * mm, "end": v(144.3, 0) * mm});
            skArc(sketch, "E15.48.0.2", {"start": v(144.6, -0.3) * mm, "mid": v(144.86, -0.94) * mm, "end": v(145.5, -1.2) * mm});
            skArc(sketch, "E15.48.0.3", {"start": v(146.4, -0.3) * mm, "mid": v(146.14, -0.94) * mm, "end": v(145.5, -1.2) * mm});
            skArc(sketch, "E15.48.0.4", {"start": v(146.4, -0.3) * mm, "mid": v(146.49, -0.09) * mm, "end": v(146.7, 0) * mm});
            skLineSegment(sketch, "E15.48.0.5", {"start": v(146.7, 0) * mm, "end": v(147, 0) * mm});
            skLineSegment(sketch, "E15.49.0.0", {"start": v(147.3, 0) * mm, "end": v(147, 0) * mm});
            skArc(sketch, "E15.49.0.1", {"start": v(147.6, -0.3) * mm, "mid": v(147.51, -0.09) * mm, "end": v(147.3, 0) * mm});
            skArc(sketch, "E15.49.0.2", {"start": v(147.6, -0.3) * mm, "mid": v(147.86, -0.94) * mm, "end": v(148.5, -1.2) * mm});
            skArc(sketch, "E15.49.0.3", {"start": v(149.4, -0.3) * mm, "mid": v(149.14, -0.94) * mm, "end": v(148.5, -1.2) * mm});
            skArc(sketch, "E15.49.0.4", {"start": v(149.4, -0.3) * mm, "mid": v(149.49, -0.09) * mm, "end": v(149.7, 0) * mm});
            skLineSegment(sketch, "E15.49.0.5", {"start": v(149.7, 0) * mm, "end": v(150, 0) * mm});
            skLineSegment(sketch, "E15.50.0.0", {"start": v(150.3, 0) * mm, "end": v(150, 0) * mm});
            skArc(sketch, "E15.50.0.1", {"start": v(150.6, -0.3) * mm, "mid": v(150.51, -0.09) * mm, "end": v(150.3, 0) * mm});
            skArc(sketch, "E15.50.0.2", {"start": v(150.6, -0.3) * mm, "mid": v(150.86, -0.94) * mm, "end": v(151.5, -1.2) * mm});
            skArc(sketch, "E15.50.0.3", {"start": v(152.4, -0.3) * mm, "mid": v(152.14, -0.94) * mm, "end": v(151.5, -1.2) * mm});
            skArc(sketch, "E15.50.0.4", {"start": v(152.4, -0.3) * mm, "mid": v(152.49, -0.09) * mm, "end": v(152.7, 0) * mm});
            skLineSegment(sketch, "E15.50.0.5", {"start": v(152.7, 0) * mm, "end": v(153, 0) * mm});
            skLineSegment(sketch, "E15.51.0.0", {"start": v(153.3, 0) * mm, "end": v(153, 0) * mm});
            skArc(sketch, "E15.51.0.1", {"start": v(153.6, -0.3) * mm, "mid": v(153.51, -0.09) * mm, "end": v(153.3, 0) * mm});
            skArc(sketch, "E15.51.0.2", {"start": v(153.6, -0.3) * mm, "mid": v(153.86, -0.94) * mm, "end": v(154.5, -1.2) * mm});
            skArc(sketch, "E15.51.0.3", {"start": v(155.4, -0.3) * mm, "mid": v(155.14, -0.94) * mm, "end": v(154.5, -1.2) * mm});
            skArc(sketch, "E15.51.0.4", {"start": v(155.4, -0.3) * mm, "mid": v(155.49, -0.09) * mm, "end": v(155.7, 0) * mm});
            skLineSegment(sketch, "E15.51.0.5", {"start": v(155.7, 0) * mm, "end": v(156, 0) * mm});
            skLineSegment(sketch, "E15.52.0.0", {"start": v(156.3, 0) * mm, "end": v(156, 0) * mm});
            skArc(sketch, "E15.52.0.1", {"start": v(156.6, -0.3) * mm, "mid": v(156.51, -0.09) * mm, "end": v(156.3, 0) * mm});
            skArc(sketch, "E15.52.0.2", {"start": v(156.6, -0.3) * mm, "mid": v(156.86, -0.94) * mm, "end": v(157.5, -1.2) * mm});
            skArc(sketch, "E15.52.0.3", {"start": v(158.4, -0.3) * mm, "mid": v(158.14, -0.94) * mm, "end": v(157.5, -1.2) * mm});
            skArc(sketch, "E15.52.0.4", {"start": v(158.4, -0.3) * mm, "mid": v(158.49, -0.09) * mm, "end": v(158.7, 0) * mm});
            skLineSegment(sketch, "E15.52.0.5", {"start": v(158.7, 0) * mm, "end": v(159, 0) * mm});
            skLineSegment(sketch, "E15.53.0.0", {"start": v(159.3, 0) * mm, "end": v(159, 0) * mm});
            skArc(sketch, "E15.53.0.1", {"start": v(159.6, -0.3) * mm, "mid": v(159.51, -0.09) * mm, "end": v(159.3, 0) * mm});
            skArc(sketch, "E15.53.0.2", {"start": v(159.6, -0.3) * mm, "mid": v(159.86, -0.94) * mm, "end": v(160.5, -1.2) * mm});
            skArc(sketch, "E15.53.0.3", {"start": v(161.4, -0.3) * mm, "mid": v(161.14, -0.94) * mm, "end": v(160.5, -1.2) * mm});
            skArc(sketch, "E15.53.0.4", {"start": v(161.4, -0.3) * mm, "mid": v(161.49, -0.09) * mm, "end": v(161.7, 0) * mm});
            skLineSegment(sketch, "E15.53.0.5", {"start": v(161.7, 0) * mm, "end": v(162, 0) * mm});
            skLineSegment(sketch, "E15.54.0.0", {"start": v(162.3, 0) * mm, "end": v(162, 0) * mm});
            skArc(sketch, "E15.54.0.1", {"start": v(162.6, -0.3) * mm, "mid": v(162.51, -0.09) * mm, "end": v(162.3, 0) * mm});
            skArc(sketch, "E15.54.0.2", {"start": v(162.6, -0.3) * mm, "mid": v(162.86, -0.94) * mm, "end": v(163.5, -1.2) * mm});
            skArc(sketch, "E15.54.0.3", {"start": v(164.4, -0.3) * mm, "mid": v(164.14, -0.94) * mm, "end": v(163.5, -1.2) * mm});
            skArc(sketch, "E15.54.0.4", {"start": v(164.4, -0.3) * mm, "mid": v(164.49, -0.09) * mm, "end": v(164.7, 0) * mm});
            skLineSegment(sketch, "E15.54.0.5", {"start": v(164.7, 0) * mm, "end": v(165, 0) * mm});
            skLineSegment(sketch, "E15.55.0.0", {"start": v(165.3, 0) * mm, "end": v(165, 0) * mm});
            skArc(sketch, "E15.55.0.1", {"start": v(165.6, -0.3) * mm, "mid": v(165.51, -0.09) * mm, "end": v(165.3, 0) * mm});
            skArc(sketch, "E15.55.0.2", {"start": v(165.6, -0.3) * mm, "mid": v(165.86, -0.94) * mm, "end": v(166.5, -1.2) * mm});
            skArc(sketch, "E15.55.0.3", {"start": v(167.4, -0.3) * mm, "mid": v(167.14, -0.94) * mm, "end": v(166.5, -1.2) * mm});
            skArc(sketch, "E15.55.0.4", {"start": v(167.4, -0.3) * mm, "mid": v(167.49, -0.09) * mm, "end": v(167.7, 0) * mm});
            skLineSegment(sketch, "E15.55.0.5", {"start": v(167.7, 0) * mm, "end": v(168, 0) * mm});
            skLineSegment(sketch, "E15.56.0.0", {"start": v(168.3, 0) * mm, "end": v(168, 0) * mm});
            skArc(sketch, "E15.56.0.1", {"start": v(168.6, -0.3) * mm, "mid": v(168.51, -0.09) * mm, "end": v(168.3, 0) * mm});
            skArc(sketch, "E15.56.0.2", {"start": v(168.6, -0.3) * mm, "mid": v(168.86, -0.94) * mm, "end": v(169.5, -1.2) * mm});
            skArc(sketch, "E15.56.0.3", {"start": v(170.4, -0.3) * mm, "mid": v(170.14, -0.94) * mm, "end": v(169.5, -1.2) * mm});
            skArc(sketch, "E15.56.0.4", {"start": v(170.4, -0.3) * mm, "mid": v(170.49, -0.09) * mm, "end": v(170.7, 0) * mm});
            skLineSegment(sketch, "E15.56.0.5", {"start": v(170.7, 0) * mm, "end": v(171, 0) * mm});
            skLineSegment(sketch, "E15.57.0.0", {"start": v(171.3, 0) * mm, "end": v(171, 0) * mm});
            skArc(sketch, "E15.57.0.1", {"start": v(171.6, -0.3) * mm, "mid": v(171.51, -0.09) * mm, "end": v(171.3, 0) * mm});
            skArc(sketch, "E15.57.0.2", {"start": v(171.6, -0.3) * mm, "mid": v(171.86, -0.94) * mm, "end": v(172.5, -1.2) * mm});
            skArc(sketch, "E15.57.0.3", {"start": v(173.4, -0.3) * mm, "mid": v(173.14, -0.94) * mm, "end": v(172.5, -1.2) * mm});
            skArc(sketch, "E15.57.0.4", {"start": v(173.4, -0.3) * mm, "mid": v(173.49, -0.09) * mm, "end": v(173.7, 0) * mm});
            skLineSegment(sketch, "E15.57.0.5", {"start": v(173.7, 0) * mm, "end": v(174, 0) * mm});
            skLineSegment(sketch, "E15.58.0.0", {"start": v(174.3, 0) * mm, "end": v(174, 0) * mm});
            skArc(sketch, "E15.58.0.1", {"start": v(174.6, -0.3) * mm, "mid": v(174.51, -0.09) * mm, "end": v(174.3, 0) * mm});
            skArc(sketch, "E15.58.0.2", {"start": v(174.6, -0.3) * mm, "mid": v(174.86, -0.94) * mm, "end": v(175.5, -1.2) * mm});
            skArc(sketch, "E15.58.0.3", {"start": v(176.4, -0.3) * mm, "mid": v(176.14, -0.94) * mm, "end": v(175.5, -1.2) * mm});
            skArc(sketch, "E15.58.0.4", {"start": v(176.4, -0.3) * mm, "mid": v(176.49, -0.09) * mm, "end": v(176.7, 0) * mm});
            skLineSegment(sketch, "E15.58.0.5", {"start": v(176.7, 0) * mm, "end": v(177, 0) * mm});
            skLineSegment(sketch, "E15.59.0.0", {"start": v(177.3, 0) * mm, "end": v(177, 0) * mm});
            skArc(sketch, "E15.59.0.1", {"start": v(177.6, -0.3) * mm, "mid": v(177.51, -0.09) * mm, "end": v(177.3, 0) * mm});
            skArc(sketch, "E15.59.0.2", {"start": v(177.6, -0.3) * mm, "mid": v(177.86, -0.94) * mm, "end": v(178.5, -1.2) * mm});
            skArc(sketch, "E15.59.0.3", {"start": v(179.4, -0.3) * mm, "mid": v(179.14, -0.94) * mm, "end": v(178.5, -1.2) * mm});
            skArc(sketch, "E15.59.0.4", {"start": v(179.4, -0.3) * mm, "mid": v(179.49, -0.09) * mm, "end": v(179.7, 0) * mm});
            skLineSegment(sketch, "E15.59.0.5", {"start": v(179.7, 0) * mm, "end": v(180, 0) * mm});
            skLineSegment(sketch, "E15.direction1", {"start": v(0.3, -0.3) * mm, "end": v(3.3, -0.3) * mm, "construction": true});
            skLineSegment(sketch, "E16.bottom", {"start": v(10, -5.1) * mm, "end": v(20, -5.1) * mm});
            skLineSegment(sketch, "E16.top", {"start": v(10, -15.1) * mm, "end": v(20, -15.1) * mm});
            skLineSegment(sketch, "E16.left", {"start": v(10, -5.1) * mm, "end": v(10, -15.1) * mm});
            skLineSegment(sketch, "E16.right", {"start": v(20, -5.1) * mm, "end": v(20, -15.1) * mm});
            skCircle(sketch, "E17", {"center": v(30, -10.1) * mm, "radius": 5.5 * mm});
            skLineSegment(sketch, "E18", {"start": v(6.77, -10.1) * mm, "end": v(42, -10.1) * mm, "construction": true});
            skCircle(sketch, "E19.1.0.0", {"center": v(50, -10.1) * mm, "radius": 5.5 * mm});
            skCircle(sketch, "E19.2.0.0", {"center": v(70, -10.1) * mm, "radius": 5.5 * mm});
            skLineSegment(sketch, "E19.direction1", {"start": v(30, -10.1) * mm, "end": v(50, -10.1) * mm, "construction": true});
            skCircle(sketch, "E20.0.3.0", {"center": v(90, -10.1) * mm, "radius": 5.5 * mm});
            skCircle(sketch, "E20.0.4.0", {"center": v(110, -10.1) * mm, "radius": 5.5 * mm});
            skCircle(sketch, "E20.0.5.0", {"center": v(130, -10.1) * mm, "radius": 5.5 * mm});
            skCircle(sketch, "E20.0.6.0", {"center": v(150, -10.1) * mm, "radius": 5.5 * mm});
            skCircle(sketch, "E21.0.7.0", {"center": v(170, -10.1) * mm, "radius": 5.5 * mm});
            skSolve(sketch);
        }
        {
            var Q0;
            Q0 = qSketchRegion(id + "F0", true);
            extrude(context, id + "F1", {"entities" : qUnion([Q0]), "depth" : 10 * mm});
        }
    });
